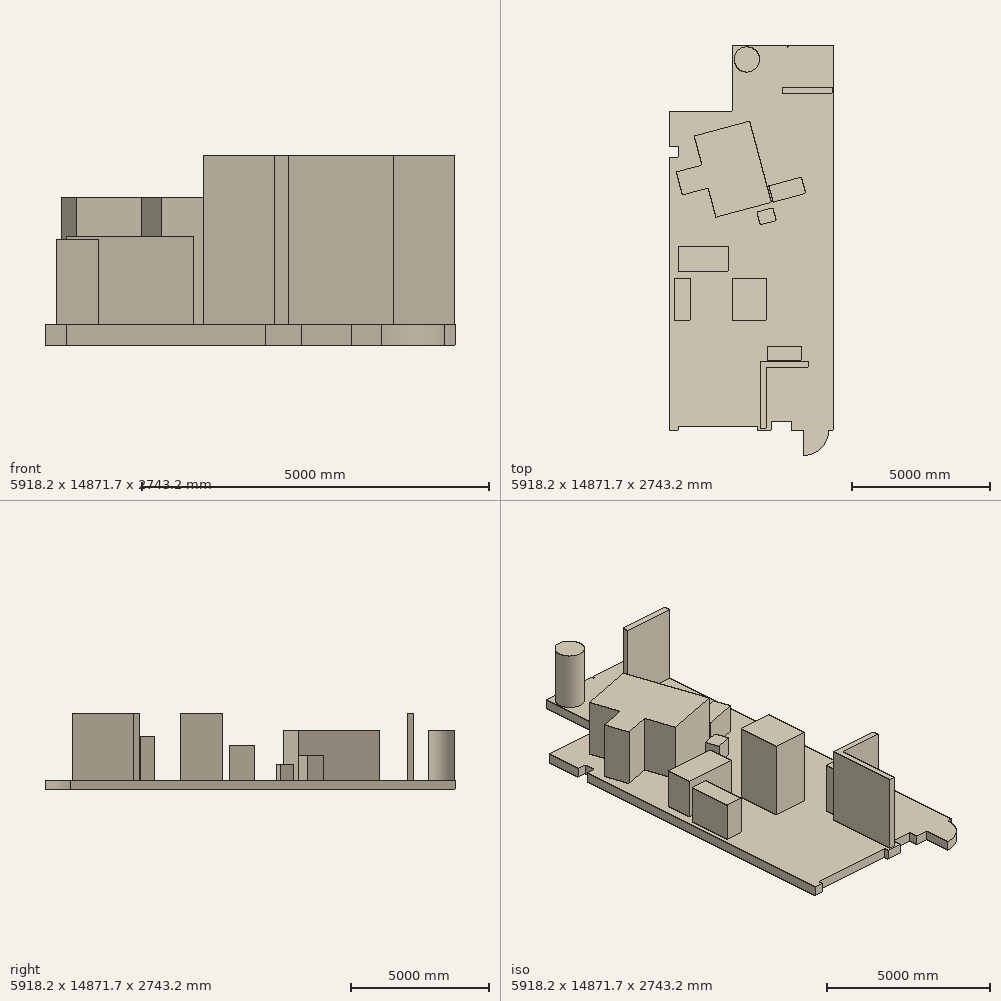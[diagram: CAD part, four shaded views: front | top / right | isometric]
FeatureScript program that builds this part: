
annotation { "Feature Type Name" : "Feature", "Feature Type Description" : "" }
export const myFeature = defineFeature(function(context is Context, id is Id, definition is map)
    precondition{}
    {
        {
            var Q0;
            Q0=qCreatedBy(makeId("Top.planeOp"),FACE);
            var sketch = newSketch(context, id + "F0", { "sketchPlane" : qUnion([Q0])});
            skLineSegment(sketch, "E0.bottom", {"start": v(-631.75, 7962.66) * mm, "end": v(1349.45, 7962.66) * mm});
            skLineSegment(sketch, "E0.top", {"start": v(-2917.75, -5994.64) * mm, "end": v(-2612.95, -5994.64) * mm});
            skLineSegment(sketch, "E0.left", {"start": v(-2917.75, 5562.36) * mm, "end": v(-2917.75, 4292.36) * mm});
            skLineSegment(sketch, "E0.right", {"start": v(3000.45, 7962.66) * mm, "end": v(3000.45, -5994.64) * mm});
            skPoint(sketch, "E0.middle", {"position": v(41.35, 984) * mm});
            skLineSegment(sketch, "E1", {"start": v(-2917.75, 5562.36) * mm, "end": v(-631.75, 5562.36) * mm});
            skLineSegment(sketch, "E2", {"start": v(-631.75, 7962.66) * mm, "end": v(-631.75, 5562.36) * mm});
            skPoint(sketch, "E3.orphan", {"position": v(-2917.75, 7962.66) * mm});
            skLineSegment(sketch, "E4.top", {"start": v(-2612.95, -5842.24) * mm, "end": v(257.25, -5842.24) * mm});
            skLineSegment(sketch, "E4.left", {"start": v(-2612.95, -5994.64) * mm, "end": v(-2612.95, -5842.24) * mm});
            skLineSegment(sketch, "E4.right", {"start": v(257.25, -5994.64) * mm, "end": v(257.25, -5842.24) * mm});
            skLineSegment(sketch, "E5", {"start": v(1933.65, -5994.64) * mm, "end": v(1933.65, -6909.04) * mm});
            skPoint(sketch, "E6", {"position": v(2848.05, -5994.64) * mm});
            skArc(sketch, "E7", {"start": v(2848.05, -5994.64) * mm, "mid": v(2580.23, -6641.22) * mm, "end": v(1933.65, -6909.04) * mm});
            skLineSegment(sketch, "E8.trimOffspring", {"start": v(2848.05, -5994.64) * mm, "end": v(3000.45, -5994.64) * mm});
            skLineSegment(sketch, "E9.trimOffspring", {"start": v(257.25, -5994.64) * mm, "end": v(777.95, -5994.64) * mm});
            skLineSegment(sketch, "E10.top", {"start": v(777.95, -5689.84) * mm, "end": v(1501.85, -5689.84) * mm});
            skLineSegment(sketch, "E10.left", {"start": v(777.95, -5994.64) * mm, "end": v(777.95, -5689.84) * mm});
            skLineSegment(sketch, "E10.right", {"start": v(1501.85, -5994.64) * mm, "end": v(1501.85, -5689.84) * mm});
            skLineSegment(sketch, "E11.top", {"start": v(1349.45, 7872.95) * mm, "end": v(1400.25, 7872.95) * mm});
            skLineSegment(sketch, "E11.left", {"start": v(1400.25, 7962.66) * mm, "end": v(1400.25, 7872.95) * mm});
            skLineSegment(sketch, "E11.right", {"start": v(1349.45, 7962.66) * mm, "end": v(1349.45, 7872.95) * mm});
            skLineSegment(sketch, "E12.bottom", {"start": v(-2917.75, 4292.36) * mm, "end": v(-2612.95, 4292.36) * mm});
            skLineSegment(sketch, "E12.top", {"start": v(-2917.75, 3898.66) * mm, "end": v(-2612.95, 3898.66) * mm});
            skLineSegment(sketch, "E12.right", {"start": v(-2612.95, 4292.36) * mm, "end": v(-2612.95, 3898.66) * mm});
            skLineSegment(sketch, "E13.trimOffspring", {"start": v(-2917.75, 3898.66) * mm, "end": v(-2917.75, -5994.64) * mm});
            skLineSegment(sketch, "E14.trimOffspring", {"start": v(1400.25, 7962.66) * mm, "end": v(3000.45, 7962.66) * mm});
            skLineSegment(sketch, "E15.trimOffspring", {"start": v(1501.85, -5994.64) * mm, "end": v(1933.65, -5994.64) * mm});
            skSolve(sketch);
        }
        {
            var Q0;
            {var subQ12=sQuery(id+"F0.wireOp",EDGE,"E0.top");Q0=makeQuery(id+"F0.imprint","IMPRINT",FACE,{"disambiguationData":[TD([[makeQuery(id+"F0.imprint","IMPRINT",EDGE,{"derivedFrom":subQ12}),1.0]])]});}
            var sketch = newSketch(context, id + "F1", { "sketchPlane" : qUnion([Q0])});
            skPoint(sketch, "E16", {"position": v(-123.75, 7454.66) * mm});
            skCircle(sketch, "E17", {"center": v(-123.75, 7454.66) * mm, "radius": 457.2 * mm});
            skLineSegment(sketch, "E18.bottom", {"start": v(-2038.13, 4675.4) * mm, "end": v(-26.3, 5214.46) * mm});
            skLineSegment(sketch, "E18.top", {"start": v(-1249.24, 1731.25) * mm, "end": v(762.59, 2270.32) * mm});
            skLineSegment(sketch, "E18.left", {"start": v(-2687.75, 3370.6) * mm, "end": v(-2464.24, 2536.43) * mm});
            skLineSegment(sketch, "E18.right", {"start": v(-26.3, 5214.46) * mm, "end": v(762.59, 2270.32) * mm});
            skPoint(sketch, "E18.middle", {"position": v(-631.75, 3428.76) * mm});
            skLineSegment(sketch, "E19.bottom", {"start": v(815.18, 2074.05) * mm, "end": v(235.56, 1918.74) * mm});
            skLineSegment(sketch, "E19.top", {"start": v(940.08, 1607.9) * mm, "end": v(360.47, 1452.58) * mm});
            skLineSegment(sketch, "E19.left", {"start": v(815.18, 2074.05) * mm, "end": v(940.08, 1607.9) * mm});
            skLineSegment(sketch, "E19.right", {"start": v(235.56, 1918.74) * mm, "end": v(360.47, 1452.58) * mm});
            skLineSegment(sketch, "E20.bottom", {"start": v(2695.65, 7963.76) * mm, "end": v(2187.65, 7963.76) * mm});
            skLineSegment(sketch, "E20.top", {"start": v(2695.65, 7354.16) * mm, "end": v(2187.65, 7354.16) * mm});
            skLineSegment(sketch, "E20.left", {"start": v(2695.65, 7963.76) * mm, "end": v(2695.65, 7354.16) * mm});
            skLineSegment(sketch, "E20.right", {"start": v(2187.65, 7963.76) * mm, "end": v(2187.65, 7354.16) * mm});
            skLineSegment(sketch, "E21.bottom", {"start": v(1070.05, 7963.76) * mm, "end": v(1679.65, 7963.76) * mm});
            skLineSegment(sketch, "E21.top", {"start": v(1070.05, 7542.33) * mm, "end": v(1679.65, 7542.33) * mm});
            skLineSegment(sketch, "E21.left", {"start": v(1070.05, 7963.76) * mm, "end": v(1070.05, 7542.33) * mm});
            skLineSegment(sketch, "E21.right", {"start": v(1679.65, 7963.76) * mm, "end": v(1679.65, 7542.33) * mm});
            skLineSegment(sketch, "E22.bottom", {"start": v(2992.16, 6427.06) * mm, "end": v(1163.36, 6427.06) * mm});
            skLineSegment(sketch, "E22.top", {"start": v(2992.16, 6223.86) * mm, "end": v(1163.36, 6223.86) * mm});
            skLineSegment(sketch, "E22.left", {"start": v(2992.16, 6427.06) * mm, "end": v(2992.16, 6223.86) * mm});
            skLineSegment(sketch, "E22.right", {"start": v(1163.36, 6427.06) * mm, "end": v(1163.36, 6223.86) * mm});
            skLineSegment(sketch, "E23.bottom", {"start": v(673.45, 2866.93) * mm, "end": v(1851.1, 3182.48) * mm});
            skLineSegment(sketch, "E23.top", {"start": v(831.23, 2278.1) * mm, "end": v(2008.89, 2593.65) * mm});
            skLineSegment(sketch, "E23.left", {"start": v(673.45, 2866.93) * mm, "end": v(831.23, 2278.1) * mm});
            skLineSegment(sketch, "E23.right", {"start": v(1851.1, 3182.48) * mm, "end": v(2008.89, 2593.65) * mm});
            skLineSegment(sketch, "E24.bottom", {"start": v(384.25, -5946.15) * mm, "end": v(587.45, -5946.15) * mm});
            skLineSegment(sketch, "E24.top", {"start": v(384.25, -3507.75) * mm, "end": v(587.45, -3507.75) * mm});
            skLineSegment(sketch, "E24.left", {"start": v(384.25, -5946.15) * mm, "end": v(384.25, -3507.75) * mm});
            skLineSegment(sketch, "E24.right", {"start": v(587.45, -5946.15) * mm, "end": v(587.45, -3710.95) * mm});
            skLineSegment(sketch, "E25", {"start": v(587.45, -3507.75) * mm, "end": v(2111.45, -3507.75) * mm});
            skLineSegment(sketch, "E26", {"start": v(2111.45, -3507.75) * mm, "end": v(2111.45, -3710.95) * mm});
            skLineSegment(sketch, "E27", {"start": v(2111.45, -3710.95) * mm, "end": v(587.45, -3710.95) * mm});
            skPoint(sketch, "E28", {"position": v(1576.38, -3253.75) * mm});
            skLineSegment(sketch, "E29.bottom", {"start": v(626.42, -2951.49) * mm, "end": v(1845.62, -2951.49) * mm});
            skLineSegment(sketch, "E29.top", {"start": v(626.42, -3459.49) * mm, "end": v(1845.62, -3459.49) * mm});
            skLineSegment(sketch, "E29.left", {"start": v(626.42, -2951.49) * mm, "end": v(626.42, -3459.49) * mm});
            skLineSegment(sketch, "E29.right", {"start": v(1845.62, -2951.49) * mm, "end": v(1845.62, -3459.49) * mm});
            skPoint(sketch, "E29.middle", {"position": v(1236.02, -3205.49) * mm});
            skLineSegment(sketch, "E30.bottom", {"start": v(-272.92, -3495.43) * mm, "end": v(336.68, -3495.43) * mm});
            skLineSegment(sketch, "E30.top", {"start": v(-272.92, -5451.23) * mm, "end": v(336.68, -5451.23) * mm});
            skLineSegment(sketch, "E30.left", {"start": v(-272.92, -3495.43) * mm, "end": v(-272.92, -5451.23) * mm});
            skLineSegment(sketch, "E30.right", {"start": v(336.68, -3495.43) * mm, "end": v(336.68, -5451.23) * mm});
            skLineSegment(sketch, "E31.bottom", {"start": v(-2612.95, 685.56) * mm, "end": v(-784.15, 685.56) * mm});
            skLineSegment(sketch, "E31.top", {"start": v(-2612.95, -228.84) * mm, "end": v(-784.15, -228.84) * mm});
            skLineSegment(sketch, "E31.left", {"start": v(-2612.95, 685.56) * mm, "end": v(-2612.95, -228.84) * mm});
            skLineSegment(sketch, "E31.right", {"start": v(-784.15, 685.56) * mm, "end": v(-784.15, -228.84) * mm});
            skPoint(sketch, "E31.middle", {"position": v(-1698.55, 228.36) * mm});
            skLineSegment(sketch, "E32.bottom", {"start": v(-2765.35, -505.46) * mm, "end": v(-2155.75, -505.46) * mm});
            skLineSegment(sketch, "E32.top", {"start": v(-2765.35, -2029.46) * mm, "end": v(-2155.75, -2029.46) * mm});
            skLineSegment(sketch, "E32.left", {"start": v(-2765.35, -505.46) * mm, "end": v(-2765.35, -2029.46) * mm});
            skLineSegment(sketch, "E32.right", {"start": v(-2155.75, -505.46) * mm, "end": v(-2155.75, -2029.46) * mm});
            skPoint(sketch, "E32.middle", {"position": v(-2460.55, -1267.46) * mm});
            skLineSegment(sketch, "E33.bottom", {"start": v(-631.75, -502.23) * mm, "end": v(587.45, -502.23) * mm});
            skLineSegment(sketch, "E33.top", {"start": v(-631.75, -2026.23) * mm, "end": v(587.45, -2026.23) * mm});
            skLineSegment(sketch, "E33.left", {"start": v(-631.75, -502.23) * mm, "end": v(-631.75, -2026.23) * mm});
            skLineSegment(sketch, "E33.right", {"start": v(587.45, -502.23) * mm, "end": v(587.45, -2026.23) * mm});
            skPoint(sketch, "E33.middle", {"position": v(-22.15, -1264.23) * mm});
            skLineSegment(sketch, "E34", {"start": v(-2687.75, 3370.6) * mm, "end": v(-1755.44, 3620.41) * mm});
            skLineSegment(sketch, "E35", {"start": v(-2464.24, 2536.43) * mm, "end": v(-1531.93, 2786.24) * mm});
            skLineSegment(sketch, "E36", {"start": v(-2038.13, 4675.4) * mm, "end": v(-1755.44, 3620.41) * mm});
            skLineSegment(sketch, "E37", {"start": v(-1249.24, 1731.25) * mm, "end": v(-1531.93, 2786.24) * mm});
            skPoint(sketch, "E38.orphan", {"position": v(-2155.75, 4952.76) * mm});
            skPoint(sketch, "E39.orphan", {"position": v(-2155.75, 1904.76) * mm});
            skLineSegment(sketch, "E40.0", {"start": v(815.18, 2074.05) * mm, "end": v(762.59, 2270.32) * mm, "construction": true});
            skSolve(sketch);
        }
        {
            var Q0;
            Q0 = qSketchRegion(id + "F0", true);
            extrude(context, id + "F2", {"entities" : qUnion([Q0]), "oppositeDirection" : true, "depth" : 304.8 * mm});
        }
        {
            var Q0;
            Q0=makeQuery(id+"F1.imprint","IMPRINT",FACE,{"disambiguationData":[TD([[makeQuery(id+"F1.imprint","IMPRINT",EDGE,{"derivedFrom":sQuery(id+"F1.wireOp",EDGE,"E18.bottom")}),-1.0]])]});
            extrude(context, id + "F3", {"entities" : qUnion([Q0]), "operationType" : NewBodyOperationType.ADD, "depth" : 1828.8 * mm});
        }
        {
            var Q0;
            Q0=makeQuery(id+"F1.imprint","IMPRINT",FACE,{"disambiguationData":[TD([[makeQuery(id+"F1.imprint","IMPRINT",EDGE,{"derivedFrom":sQuery(id+"F1.wireOp",EDGE,"E23.bottom")}),-1.0]])]});
            extrude(context, id + "F4", {"entities" : qUnion([Q0]), "operationType" : NewBodyOperationType.ADD, "depth" : 914.4 * mm});
        }
        {
            var Q0;
            Q0=makeQuery(id+"F1.imprint","IMPRINT",FACE,{"disambiguationData":[TD([[makeQuery(id+"F1.imprint","IMPRINT",EDGE,{"derivedFrom":sQuery(id+"F1.wireOp",EDGE,"E19.bottom")}),1.0]])]});
            extrude(context, id + "F5", {"entities" : qUnion([Q0]), "operationType" : NewBodyOperationType.ADD, "depth" : 609.6 * mm});
        }
        {
            var Q0;
            Q0=makeQuery(id+"F1.imprint","IMPRINT",FACE,{"disambiguationData":[TD([[makeQuery(id+"F1.imprint","IMPRINT",EDGE,{"derivedFrom":sQuery(id+"F1.wireOp",EDGE,"E24.bottom")}),1.0]])]});
            extrude(context, id + "F6", {"entities" : qUnion([Q0]), "operationType" : NewBodyOperationType.ADD, "depth" : 2438.4 * mm});
        }
        {
            var Q0;
            Q0=makeQuery(id+"F1.imprint","IMPRINT",FACE,{"disambiguationData":[TD([[makeQuery(id+"F1.imprint","IMPRINT",EDGE,{"derivedFrom":sQuery(id+"F1.wireOp",EDGE,"E22.bottom")}),1.0]])]});
            extrude(context, id + "F7", {"entities" : qUnion([Q0]), "operationType" : NewBodyOperationType.ADD, "depth" : 2438.4 * mm});
        }
        {
            var Q0;
            Q0=makeQuery(id+"F1.imprint","IMPRINT",FACE,{"disambiguationData":[TD([[makeQuery(id+"F1.imprint","IMPRINT",EDGE,{"derivedFrom":sQuery(id+"F1.wireOp",EDGE,"E17")}),1.0]])]});
            extrude(context, id + "F8", {"entities" : qUnion([Q0]), "operationType" : NewBodyOperationType.ADD, "depth" : 1828.8 * mm});
        }
        {
            var Q0;
            Q0=sQuery(id+"F1.wireOp",EDGE,"E30.bottom");
            var Q1;
            Q1=sQuery(id+"F1.wireOp",EDGE,"E30.left");
            var Q2;
            Q2=sQuery(id+"F1.wireOp",EDGE,"E30.top");
            var Q3;
            Q3=sQuery(id+"F1.wireOp",EDGE,"E30.right");
            extrude(context, id + "F9", {"bodyType" : ToolBodyType.SURFACE, "surfaceEntities" : qUnion([Q0, Q1, Q2, Q3]), "depth" : 1981.2 * mm});
        }
        {
            var Q0;
            Q0=makeQuery(id+"F1.imprint","IMPRINT",FACE,{"disambiguationData":[TD([[makeQuery(id+"F1.imprint","IMPRINT",EDGE,{"derivedFrom":sQuery(id+"F1.wireOp",EDGE,"E33.bottom")}),-1.0]])]});
            extrude(context, id + "F10", {"entities" : qUnion([Q0]), "operationType" : NewBodyOperationType.ADD, "depth" : 2438.4 * mm});
        }
        {
            var Q0;
            Q0=makeQuery(id+"F1.imprint","IMPRINT",FACE,{"disambiguationData":[TD([[makeQuery(id+"F1.imprint","IMPRINT",EDGE,{"derivedFrom":sQuery(id+"F1.wireOp",EDGE,"E32.bottom")}),-1.0]])]});
            extrude(context, id + "F11", {"entities" : qUnion([Q0]), "operationType" : NewBodyOperationType.ADD, "depth" : 1219.2 * mm});
        }
        {
            var Q0;
            Q0=makeQuery(id+"F1.imprint","IMPRINT",FACE,{"disambiguationData":[TD([[makeQuery(id+"F1.imprint","IMPRINT",EDGE,{"derivedFrom":sQuery(id+"F1.wireOp",EDGE,"E31.bottom")}),-1.0]])]});
            extrude(context, id + "F12", {"entities" : qUnion([Q0]), "operationType" : NewBodyOperationType.ADD, "depth" : 1270 * mm});
        }
        {
            var Q0;
            Q0=makeQuery(id+"F1.imprint","IMPRINT",FACE,{"disambiguationData":[TD([[makeQuery(id+"F1.imprint","IMPRINT",EDGE,{"derivedFrom":sQuery(id+"F1.wireOp",EDGE,"E29.bottom")}),-1.0]])]});
            extrude(context, id + "F13", {"entities" : qUnion([Q0]), "operationType" : NewBodyOperationType.ADD, "depth" : 1625.6 * mm});
        }
    });
